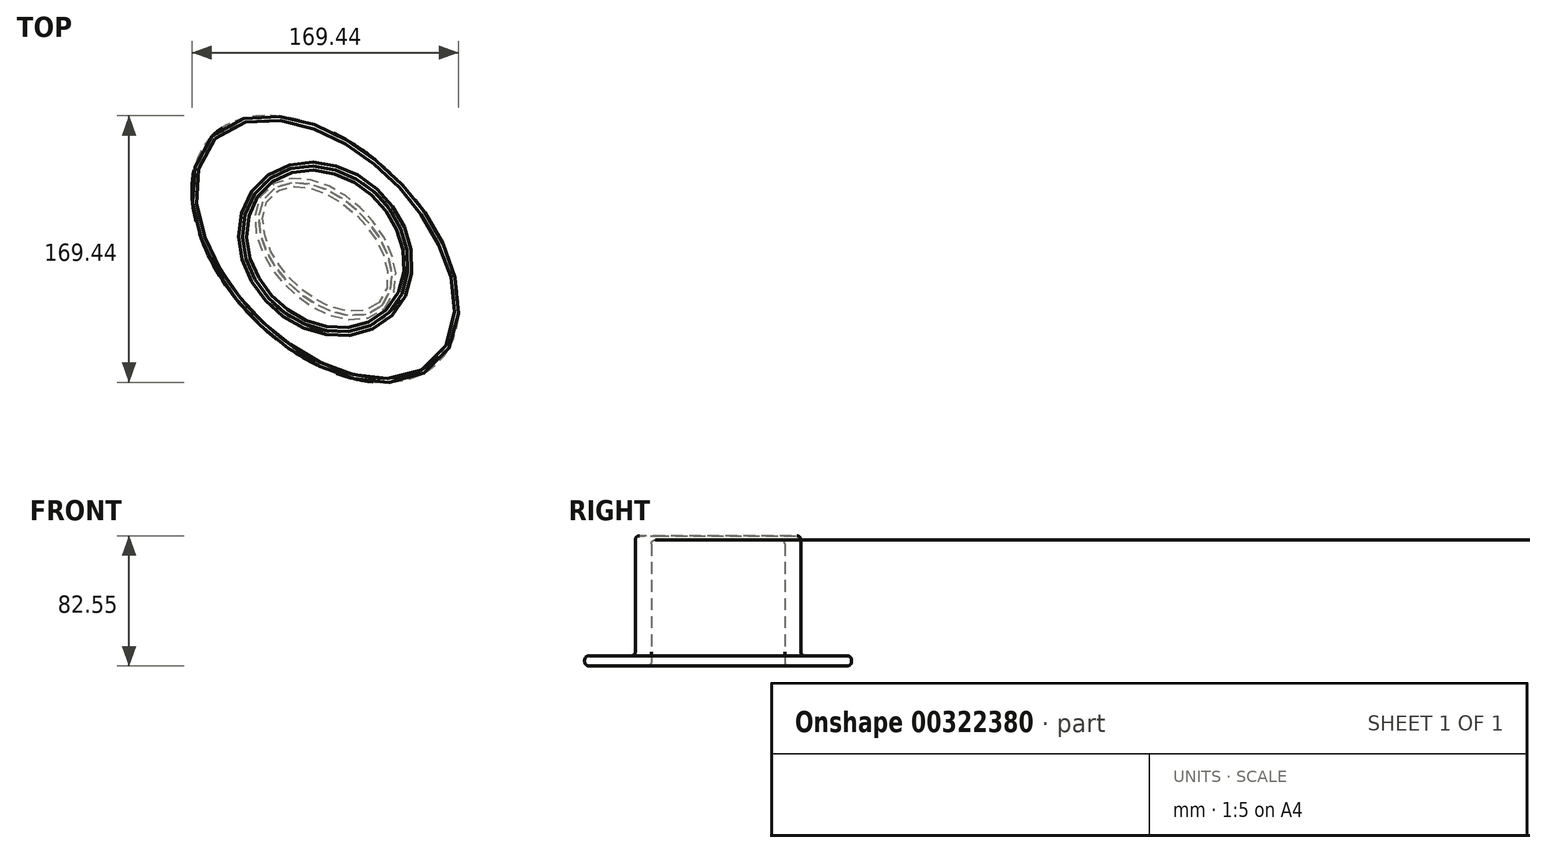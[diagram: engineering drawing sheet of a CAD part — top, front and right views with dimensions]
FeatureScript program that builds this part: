
annotation { "Feature Type Name" : "Feature", "Feature Type Description" : "" }
export const myFeature = defineFeature(function(context is Context, id is Id, definition is map)
    precondition{}
    {
        {
            var Q0;
            Q0=qCreatedBy(makeId("Top.planeOp"),FACE);
            var sketch = newSketch(context, id + "F0", { "sketchPlane" : qUnion([Q0])});
            skEllipse(sketch, "E0", {"center": v(0, 0) * mm, "majorRadius": 101.6 * mm, "minorRadius": 63.5 * mm, "majorAxis": v(-0.7, 0.7)});
            skLineSegment(sketch, "E1", {"start": v(-71.84, 71.84) * mm, "end": v(71.84, -71.84) * mm});
            skSolve(sketch);
        }
        {
            var Q0;
            Q0=makeQuery(id+"F0.imprint","IMPRINT",FACE,{"disambiguationData":[TD([[makeQuery(id+"F0.imprint","IMPRINT",EDGE,{"derivedFrom":sQuery(id+"F0.wireOp",EDGE,"E0")}),1.0]])]});
            extrude(context, id + "F1", {"entities" : qUnion([Q0]), "depth" : 6.35 * mm});
        }
        {
            var Q0;
            Q0=qCreatedBy(makeId("Top.planeOp"),FACE);
            var sketch = newSketch(context, id + "F2", { "sketchPlane" : qUnion([Q0])});
            skEllipse(sketch, "E2", {"center": v(0, 0) * mm, "majorRadius": 50.8 * mm, "minorRadius": 31.75 * mm, "majorAxis": v(0.7, -0.7)});
            skLineSegment(sketch, "E3", {"start": v(-35.92, 35.92) * mm, "end": v(35.92, -35.92) * mm});
            skSolve(sketch);
        }
        {
            var Q0;
            Q0=makeQuery(id+"F1.opExtrude","CAP_FACE",FACE,{"disambiguationData":[OSD([sQuery(id+"F0.wireOp",EDGE,"E0")])],"isStart":false});
            var sketch = newSketch(context, id + "F3", { "sketchPlane" : qUnion([Q0])});
            skEllipse(sketch, "E4", {"center": v(0, 0) * mm, "majorRadius": 57.15 * mm, "minorRadius": 47.63 * mm, "majorAxis": v(0.7, -0.7)});
            skLineSegment(sketch, "E5", {"start": v(-40.41, 40.41) * mm, "end": v(40.41, -40.41) * mm});
            skSolve(sketch);
        }
        {
            var Q0;
            Q0 = qSketchRegion(id + "F3", true);
            extrude(context, id + "F4", {"entities" : qUnion([Q0]), "operationType" : NewBodyOperationType.ADD, "depth" : 76.2 * mm});
        }
        {
            var Q0;
            Q0 = qSketchRegion(id + "F2", true);
            extrude(context, id + "F5", {"entities" : qUnion([Q0]), "operationType" : NewBodyOperationType.REMOVE, "depth" : 80 * mm});
        }
        {
            var Q0;
            Q0=makeQuery(id+"F4.opExtrude","SWEPT_FACE",FACE,{"disambiguationData":[OSD([sQuery(id+"F3.wireOp",EDGE,"E4")])]});
            var Q1;
            Q1=makeQuery(id+"F1.opExtrude","CAP_EDGE",EDGE,{"disambiguationData":[OSD([sQuery(id+"F0.wireOp",EDGE,"E0")])],"isStart":false});
            var Q2;
            Q2=makeQuery(id+"F1.opExtrude","SWEPT_FACE",FACE,{"disambiguationData":[OSD([sQuery(id+"F0.wireOp",EDGE,"E0")])]});
            var Q3;
            Q3=makeQuery(id+"F4.opExtrude","CAP_EDGE",EDGE,{"disambiguationData":[OSD([sQuery(id+"F3.wireOp",EDGE,"E4")])],"isStart":false});
            var Q4;
            Q4=makeQuery(id+"F4.opExtrude","CAP_FACE",FACE,{"disambiguationData":[OSD([sQuery(id+"F3.wireOp",EDGE,"E4")])],"isStart":false});
            var Q5;
            Q5=makeQuery(id+"F4.opExtrude","CAP_EDGE",EDGE,{"disambiguationData":[OSD([sQuery(id+"F3.wireOp",EDGE,"E4")])],"isStart":true});
            var Q6;
            Q6=makeQuery(id+"F1.opExtrude","CAP_FACE",FACE,{"disambiguationData":[OSD([sQuery(id+"F0.wireOp",EDGE,"E0")])],"isStart":false});
            var Q7;
            Q7=makeQuery(id+"F5.boolean.opBoolean","COPY",EDGE,{"derivedFrom":makeQuery(id+"F5.opExtrude","CAP_EDGE",EDGE,{"disambiguationData":[OSD([sQuery(id+"F2.wireOp",EDGE,"E2")])],"isStart":true})});
            var Q8;
            Q8=makeQuery(id+"F1.opExtrude","CAP_EDGE",EDGE,{"disambiguationData":[OSD([sQuery(id+"F0.wireOp",EDGE,"E0")])],"isStart":true});
            var Q9;
            Q9=makeQuery(id+"F5.boolean.opBoolean","COPY",FACE,{"derivedFrom":makeQuery(id+"F5.opExtrude","SWEPT_FACE",FACE,{"disambiguationData":[OSD([sQuery(id+"F2.wireOp",EDGE,"E2")])]})});
            var Q10;
            Q10=makeQuery(id+"F5.boolean.opBoolean","COPY",EDGE,{"derivedFrom":makeQuery(id+"F5.opExtrude","CAP_EDGE",EDGE,{"disambiguationData":[OSD([sQuery(id+"F2.wireOp",EDGE,"E2")])],"isStart":false})});
            var Q11;
            Q11=makeQuery(id+"F5.boolean.opBoolean","COPY",FACE,{"derivedFrom":makeQuery(id+"F5.opExtrude","CAP_FACE",FACE,{"disambiguationData":[OSD([sQuery(id+"F2.wireOp",EDGE,"E2")])],"isStart":false})});
            var Q12;
            Q12=makeQuery(id+"F1.opExtrude","CAP_FACE",FACE,{"disambiguationData":[OSD([sQuery(id+"F0.wireOp",EDGE,"E0")])],"isStart":true});
            fillet(context, id + "F6", {"entities" : qUnion([Q0, Q1, Q2, Q3, Q4, Q5, Q6, Q7, Q8, Q9, Q10, Q11, Q12]), "radius" : 2.54 * mm, "tangentPropagation" : true, "allowEdgeOverflow" : false});
        }
    });
